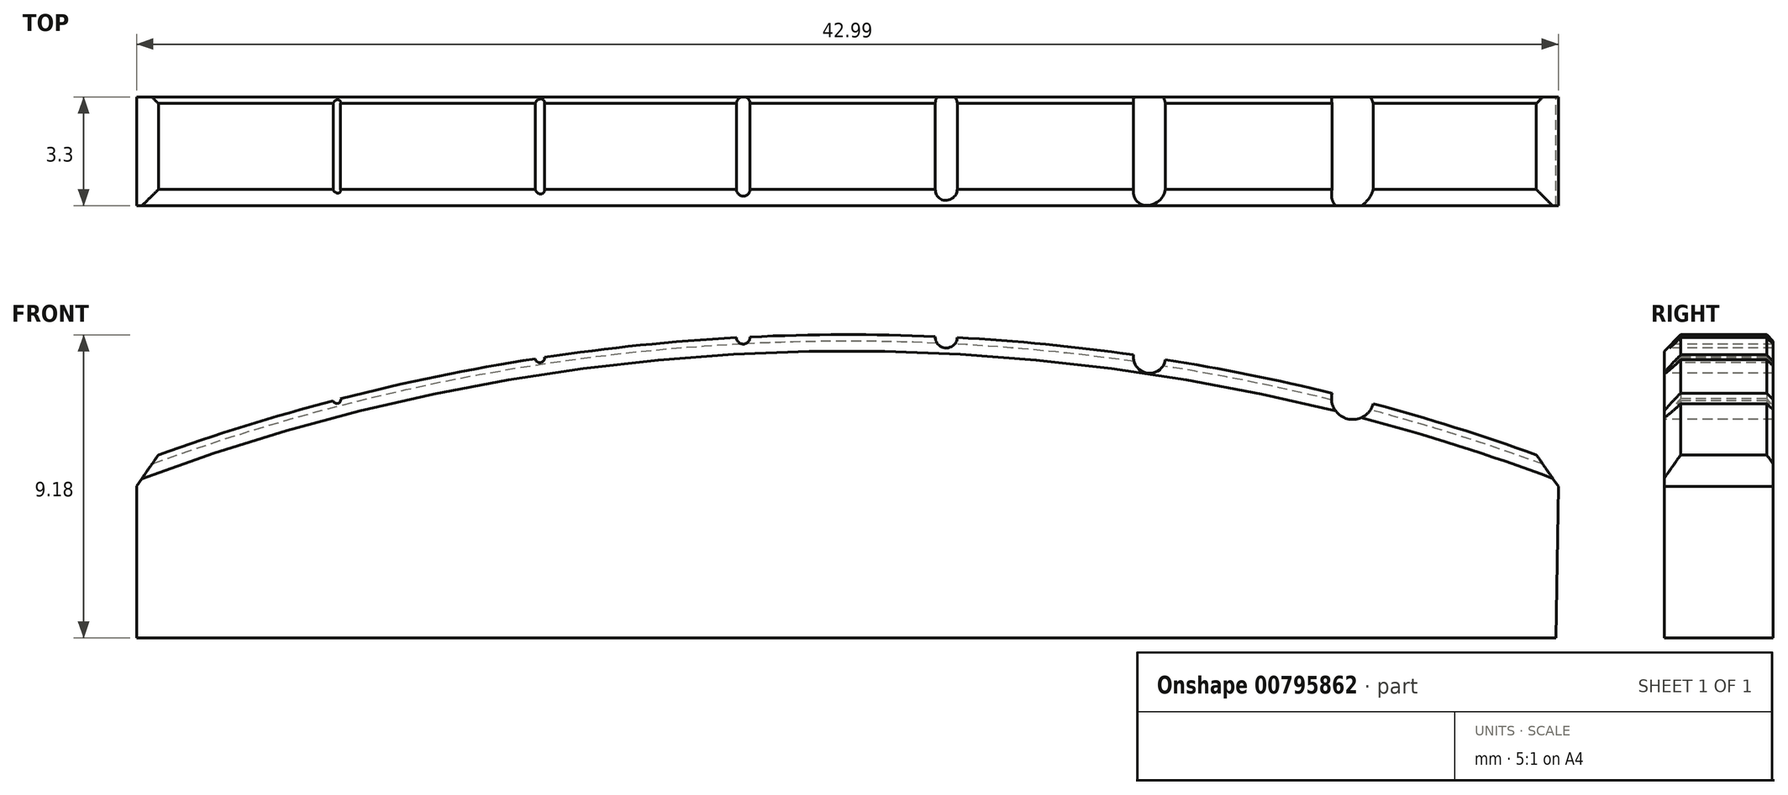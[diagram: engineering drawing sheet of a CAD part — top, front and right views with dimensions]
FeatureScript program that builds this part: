
annotation { "Feature Type Name" : "Feature", "Feature Type Description" : "" }
export const myFeature = defineFeature(function(context is Context, id is Id, definition is map)
    precondition{}
    {
        {
            var Q0;
            Q0=qCreatedBy(makeId("Front.planeOp"),FACE);
            var sketch = newSketch(context, id + "F0", { "sketchPlane" : qUnion([Q0])});
            skArc(sketch, "E0", {"start": v(-21.5, 5.3) * mm, "mid": v(0, 9.18) * mm, "end": v(21.5, 5.3) * mm});
            skLineSegment(sketch, "E1", {"start": v(-21.5, 5.3) * mm, "end": v(-21.5, 0) * mm});
            skLineSegment(sketch, "E2", {"start": v(-21.5, 0) * mm, "end": v(21.41, 0) * mm});
            skLineSegment(sketch, "E3", {"start": v(21.41, 0) * mm, "end": v(21.5, 5.3) * mm});
            skSolve(sketch);
        }
        {
            var Q0;
            Q0 = qSketchRegion(id + "F0", true);
            extrude(context, id + "F1", {"entities" : qUnion([Q0]), "depth" : 3.3 * mm, "offsetDistance" : 25 * mm});
        }
        {
            var Q0;
            Q0=makeQuery(id+"F1.opExtrude","CAP_FACE",FACE,{"disambiguationData":[OSD([sQuery(id+"F0.wireOp",EDGE,"E0"),sQuery(id+"F0.wireOp",EDGE,"E1"),sQuery(id+"F0.wireOp",EDGE,"E2"),sQuery(id+"F0.wireOp",EDGE,"E3")])],"isStart":false});
            var sketch = newSketch(context, id + "F2", { "sketchPlane" : qUnion([Q0])});
            skCircle(sketch, "E4", {"center": v(-15.44, 7.21) * mm, "radius": 0.12 * mm});
            skCircle(sketch, "E5", {"center": v(-9.3, 8.48) * mm, "radius": 0.14 * mm});
            skCircle(sketch, "E6", {"center": v(-3.16, 9.1) * mm, "radius": 0.2 * mm});
            skCircle(sketch, "E7", {"center": v(2.99, 9.11) * mm, "radius": 0.33 * mm});
            skCircle(sketch, "E8", {"center": v(9.13, 8.5) * mm, "radius": 0.49 * mm});
            skCircle(sketch, "E9", {"center": v(15.27, 7.26) * mm, "radius": 0.64 * mm});
            skLineSegment(sketch, "E10", {"start": v(-15.44, 7.21) * mm, "end": v(-15.44, 0) * mm, "construction": true});
            skLineSegment(sketch, "E11", {"start": v(-9.3, 8.48) * mm, "end": v(-9.3, 0) * mm, "construction": true});
            skLineSegment(sketch, "E12", {"start": v(-3.16, 9.1) * mm, "end": v(-3.16, 0) * mm, "construction": true});
            skLineSegment(sketch, "E13", {"start": v(2.99, 9.11) * mm, "end": v(2.99, 0) * mm, "construction": true});
            skLineSegment(sketch, "E14", {"start": v(9.13, 8.5) * mm, "end": v(9.13, 0) * mm, "construction": true});
            skLineSegment(sketch, "E15", {"start": v(15.27, 7.26) * mm, "end": v(15.27, 0) * mm, "construction": true});
            skSolve(sketch);
        }
        {
            var Q0;
            Q0 = qSketchRegion(id + "F2", true);
            extrude(context, id + "F3", {"entities" : qUnion([Q0]), "operationType" : NewBodyOperationType.REMOVE, "oppositeDirection" : true, "depth" : 25 * mm, "offsetDistance" : 25 * mm});
        }
        {
            var Q0;
            {var subQ0=sQuery(id+"F0.wireOp",EDGE,"E0");var subQ1=sQuery(id+"F0.wireOp",EDGE,"E1");Q0=makeQuery(id+"F3.boolean.opBoolean","SPLIT",EDGE,{"disambiguationData":[TD([makeQuery(id+"F1.opExtrude","SWEPT_FACE",FACE,{"disambiguationData":[OSD([subQ0])]}),makeQuery(id+"F1.opExtrude","CAP_FACE",FACE,{"disambiguationData":[OSD([subQ0,subQ1,sQuery(id+"F0.wireOp",EDGE,"E2"),sQuery(id+"F0.wireOp",EDGE,"E3")])],"isStart":false}),makeQuery(id+"F1.opExtrude","SWEPT_FACE",FACE,{"disambiguationData":[OSD([subQ1])]}),makeQuery(id+"F3.opExtrude","SWEPT_FACE",FACE,{"disambiguationData":[OSD([sQuery(id+"F2.wireOp",EDGE,"E4")])]})])],"derivedFrom":makeQuery(id+"F1.opExtrude","CAP_EDGE",EDGE,{"disambiguationData":[OSD([subQ0])],"isStart":false})});}
            var Q1;
            {var subQ0=sQuery(id+"F0.wireOp",EDGE,"E0");Q1=makeQuery(id+"F3.boolean.opBoolean","SPLIT",EDGE,{"disambiguationData":[TD([makeQuery(id+"F1.opExtrude","SWEPT_FACE",FACE,{"disambiguationData":[OSD([subQ0])]}),makeQuery(id+"F1.opExtrude","CAP_FACE",FACE,{"disambiguationData":[OSD([subQ0,sQuery(id+"F0.wireOp",EDGE,"E1"),sQuery(id+"F0.wireOp",EDGE,"E2"),sQuery(id+"F0.wireOp",EDGE,"E3")])],"isStart":false}),makeQuery(id+"F3.opExtrude","SWEPT_FACE",FACE,{"disambiguationData":[OSD([sQuery(id+"F2.wireOp",EDGE,"E4")])]}),makeQuery(id+"F3.opExtrude","SWEPT_FACE",FACE,{"disambiguationData":[OSD([sQuery(id+"F2.wireOp",EDGE,"E5")])]})])],"derivedFrom":makeQuery(id+"F1.opExtrude","CAP_EDGE",EDGE,{"disambiguationData":[OSD([subQ0])],"isStart":false})});}
            var Q2;
            {var subQ0=sQuery(id+"F0.wireOp",EDGE,"E0");Q2=makeQuery(id+"F3.boolean.opBoolean","SPLIT",EDGE,{"disambiguationData":[TD([makeQuery(id+"F1.opExtrude","SWEPT_FACE",FACE,{"disambiguationData":[OSD([subQ0])]}),makeQuery(id+"F1.opExtrude","CAP_FACE",FACE,{"disambiguationData":[OSD([subQ0,sQuery(id+"F0.wireOp",EDGE,"E1"),sQuery(id+"F0.wireOp",EDGE,"E2"),sQuery(id+"F0.wireOp",EDGE,"E3")])],"isStart":false}),makeQuery(id+"F3.opExtrude","SWEPT_FACE",FACE,{"disambiguationData":[OSD([sQuery(id+"F2.wireOp",EDGE,"E5")])]}),makeQuery(id+"F3.opExtrude","SWEPT_FACE",FACE,{"disambiguationData":[OSD([sQuery(id+"F2.wireOp",EDGE,"E6")])]})])],"derivedFrom":makeQuery(id+"F1.opExtrude","CAP_EDGE",EDGE,{"disambiguationData":[OSD([subQ0])],"isStart":false})});}
            var Q3;
            {var subQ0=sQuery(id+"F0.wireOp",EDGE,"E0");Q3=makeQuery(id+"F3.boolean.opBoolean","SPLIT",EDGE,{"disambiguationData":[TD([makeQuery(id+"F1.opExtrude","SWEPT_FACE",FACE,{"disambiguationData":[OSD([subQ0])]}),makeQuery(id+"F1.opExtrude","CAP_FACE",FACE,{"disambiguationData":[OSD([subQ0,sQuery(id+"F0.wireOp",EDGE,"E1"),sQuery(id+"F0.wireOp",EDGE,"E2"),sQuery(id+"F0.wireOp",EDGE,"E3")])],"isStart":false}),makeQuery(id+"F3.opExtrude","SWEPT_FACE",FACE,{"disambiguationData":[OSD([sQuery(id+"F2.wireOp",EDGE,"E6")])]}),makeQuery(id+"F3.opExtrude","SWEPT_FACE",FACE,{"disambiguationData":[OSD([sQuery(id+"F2.wireOp",EDGE,"E7")])]})])],"derivedFrom":makeQuery(id+"F1.opExtrude","CAP_EDGE",EDGE,{"disambiguationData":[OSD([subQ0])],"isStart":false})});}
            var Q4;
            {var subQ0=sQuery(id+"F0.wireOp",EDGE,"E0");Q4=makeQuery(id+"F3.boolean.opBoolean","SPLIT",EDGE,{"disambiguationData":[TD([makeQuery(id+"F1.opExtrude","SWEPT_FACE",FACE,{"disambiguationData":[OSD([subQ0])]}),makeQuery(id+"F1.opExtrude","CAP_FACE",FACE,{"disambiguationData":[OSD([subQ0,sQuery(id+"F0.wireOp",EDGE,"E1"),sQuery(id+"F0.wireOp",EDGE,"E2"),sQuery(id+"F0.wireOp",EDGE,"E3")])],"isStart":false}),makeQuery(id+"F3.opExtrude","SWEPT_FACE",FACE,{"disambiguationData":[OSD([sQuery(id+"F2.wireOp",EDGE,"E7")])]}),makeQuery(id+"F3.opExtrude","SWEPT_FACE",FACE,{"disambiguationData":[OSD([sQuery(id+"F2.wireOp",EDGE,"E8")])]})])],"derivedFrom":makeQuery(id+"F1.opExtrude","CAP_EDGE",EDGE,{"disambiguationData":[OSD([subQ0])],"isStart":false})});}
            var Q5;
            {var subQ0=sQuery(id+"F0.wireOp",EDGE,"E0");Q5=makeQuery(id+"F3.boolean.opBoolean","SPLIT",EDGE,{"disambiguationData":[TD([makeQuery(id+"F1.opExtrude","SWEPT_FACE",FACE,{"disambiguationData":[OSD([subQ0])]}),makeQuery(id+"F1.opExtrude","CAP_FACE",FACE,{"disambiguationData":[OSD([subQ0,sQuery(id+"F0.wireOp",EDGE,"E1"),sQuery(id+"F0.wireOp",EDGE,"E2"),sQuery(id+"F0.wireOp",EDGE,"E3")])],"isStart":false}),makeQuery(id+"F3.opExtrude","SWEPT_FACE",FACE,{"disambiguationData":[OSD([sQuery(id+"F2.wireOp",EDGE,"E8")])]}),makeQuery(id+"F3.opExtrude","SWEPT_FACE",FACE,{"disambiguationData":[OSD([sQuery(id+"F2.wireOp",EDGE,"E9")])]})])],"derivedFrom":makeQuery(id+"F1.opExtrude","CAP_EDGE",EDGE,{"disambiguationData":[OSD([subQ0])],"isStart":false})});}
            var Q6;
            {var subQ0=sQuery(id+"F0.wireOp",EDGE,"E0");var subQ1=sQuery(id+"F0.wireOp",EDGE,"E3");Q6=makeQuery(id+"F3.boolean.opBoolean","SPLIT",EDGE,{"disambiguationData":[TD([makeQuery(id+"F1.opExtrude","SWEPT_FACE",FACE,{"disambiguationData":[OSD([subQ0])]}),makeQuery(id+"F1.opExtrude","CAP_FACE",FACE,{"disambiguationData":[OSD([subQ0,sQuery(id+"F0.wireOp",EDGE,"E1"),sQuery(id+"F0.wireOp",EDGE,"E2"),subQ1])],"isStart":false}),makeQuery(id+"F1.opExtrude","SWEPT_FACE",FACE,{"disambiguationData":[OSD([subQ1])]}),makeQuery(id+"F3.opExtrude","SWEPT_FACE",FACE,{"disambiguationData":[OSD([sQuery(id+"F2.wireOp",EDGE,"E9")])]})])],"derivedFrom":makeQuery(id+"F1.opExtrude","CAP_EDGE",EDGE,{"disambiguationData":[OSD([subQ0])],"isStart":false})});}
            chamfer(context, id + "F4", {"entities" : qUnion([Q0, Q1, Q2, Q3, Q4, Q5, Q6]), "width" : 0.5 * mm, "tangentPropagation" : true});
        }
        {
            var Q0;
            {var subQ0=sQuery(id+"F0.wireOp",EDGE,"E0");var subQ1=sQuery(id+"F0.wireOp",EDGE,"E3");Q0=makeQuery(id+"F3.boolean.opBoolean","SPLIT",EDGE,{"disambiguationData":[TD([makeQuery(id+"F1.opExtrude","SWEPT_FACE",FACE,{"disambiguationData":[OSD([subQ0])]}),makeQuery(id+"F1.opExtrude","CAP_FACE",FACE,{"disambiguationData":[OSD([subQ0,sQuery(id+"F0.wireOp",EDGE,"E1"),sQuery(id+"F0.wireOp",EDGE,"E2"),subQ1])],"isStart":true}),makeQuery(id+"F1.opExtrude","SWEPT_FACE",FACE,{"disambiguationData":[OSD([subQ1])]}),makeQuery(id+"F3.opExtrude","SWEPT_FACE",FACE,{"disambiguationData":[OSD([sQuery(id+"F2.wireOp",EDGE,"E9")])]})])],"derivedFrom":makeQuery(id+"F1.opExtrude","CAP_EDGE",EDGE,{"disambiguationData":[OSD([subQ0])],"isStart":true})});}
            var Q1;
            {var subQ0=sQuery(id+"F0.wireOp",EDGE,"E0");Q1=makeQuery(id+"F3.boolean.opBoolean","SPLIT",EDGE,{"disambiguationData":[TD([makeQuery(id+"F1.opExtrude","SWEPT_FACE",FACE,{"disambiguationData":[OSD([subQ0])]}),makeQuery(id+"F1.opExtrude","CAP_FACE",FACE,{"disambiguationData":[OSD([subQ0,sQuery(id+"F0.wireOp",EDGE,"E1"),sQuery(id+"F0.wireOp",EDGE,"E2"),sQuery(id+"F0.wireOp",EDGE,"E3")])],"isStart":true}),makeQuery(id+"F3.opExtrude","SWEPT_FACE",FACE,{"disambiguationData":[OSD([sQuery(id+"F2.wireOp",EDGE,"E8")])]}),makeQuery(id+"F3.opExtrude","SWEPT_FACE",FACE,{"disambiguationData":[OSD([sQuery(id+"F2.wireOp",EDGE,"E9")])]})])],"derivedFrom":makeQuery(id+"F1.opExtrude","CAP_EDGE",EDGE,{"disambiguationData":[OSD([subQ0])],"isStart":true})});}
            var Q2;
            {var subQ0=sQuery(id+"F0.wireOp",EDGE,"E0");Q2=makeQuery(id+"F3.boolean.opBoolean","SPLIT",EDGE,{"disambiguationData":[TD([makeQuery(id+"F1.opExtrude","SWEPT_FACE",FACE,{"disambiguationData":[OSD([subQ0])]}),makeQuery(id+"F1.opExtrude","CAP_FACE",FACE,{"disambiguationData":[OSD([subQ0,sQuery(id+"F0.wireOp",EDGE,"E1"),sQuery(id+"F0.wireOp",EDGE,"E2"),sQuery(id+"F0.wireOp",EDGE,"E3")])],"isStart":true}),makeQuery(id+"F3.opExtrude","SWEPT_FACE",FACE,{"disambiguationData":[OSD([sQuery(id+"F2.wireOp",EDGE,"E7")])]}),makeQuery(id+"F3.opExtrude","SWEPT_FACE",FACE,{"disambiguationData":[OSD([sQuery(id+"F2.wireOp",EDGE,"E8")])]})])],"derivedFrom":makeQuery(id+"F1.opExtrude","CAP_EDGE",EDGE,{"disambiguationData":[OSD([subQ0])],"isStart":true})});}
            var Q3;
            {var subQ0=sQuery(id+"F0.wireOp",EDGE,"E0");Q3=makeQuery(id+"F3.boolean.opBoolean","SPLIT",EDGE,{"disambiguationData":[TD([makeQuery(id+"F1.opExtrude","SWEPT_FACE",FACE,{"disambiguationData":[OSD([subQ0])]}),makeQuery(id+"F1.opExtrude","CAP_FACE",FACE,{"disambiguationData":[OSD([subQ0,sQuery(id+"F0.wireOp",EDGE,"E1"),sQuery(id+"F0.wireOp",EDGE,"E2"),sQuery(id+"F0.wireOp",EDGE,"E3")])],"isStart":true}),makeQuery(id+"F3.opExtrude","SWEPT_FACE",FACE,{"disambiguationData":[OSD([sQuery(id+"F2.wireOp",EDGE,"E6")])]}),makeQuery(id+"F3.opExtrude","SWEPT_FACE",FACE,{"disambiguationData":[OSD([sQuery(id+"F2.wireOp",EDGE,"E7")])]})])],"derivedFrom":makeQuery(id+"F1.opExtrude","CAP_EDGE",EDGE,{"disambiguationData":[OSD([subQ0])],"isStart":true})});}
            var Q4;
            {var subQ0=sQuery(id+"F0.wireOp",EDGE,"E0");Q4=makeQuery(id+"F3.boolean.opBoolean","SPLIT",EDGE,{"disambiguationData":[TD([makeQuery(id+"F1.opExtrude","SWEPT_FACE",FACE,{"disambiguationData":[OSD([subQ0])]}),makeQuery(id+"F1.opExtrude","CAP_FACE",FACE,{"disambiguationData":[OSD([subQ0,sQuery(id+"F0.wireOp",EDGE,"E1"),sQuery(id+"F0.wireOp",EDGE,"E2"),sQuery(id+"F0.wireOp",EDGE,"E3")])],"isStart":true}),makeQuery(id+"F3.opExtrude","SWEPT_FACE",FACE,{"disambiguationData":[OSD([sQuery(id+"F2.wireOp",EDGE,"E5")])]}),makeQuery(id+"F3.opExtrude","SWEPT_FACE",FACE,{"disambiguationData":[OSD([sQuery(id+"F2.wireOp",EDGE,"E6")])]})])],"derivedFrom":makeQuery(id+"F1.opExtrude","CAP_EDGE",EDGE,{"disambiguationData":[OSD([subQ0])],"isStart":true})});}
            var Q5;
            {var subQ0=sQuery(id+"F0.wireOp",EDGE,"E0");Q5=makeQuery(id+"F3.boolean.opBoolean","SPLIT",EDGE,{"disambiguationData":[TD([makeQuery(id+"F1.opExtrude","SWEPT_FACE",FACE,{"disambiguationData":[OSD([subQ0])]}),makeQuery(id+"F1.opExtrude","CAP_FACE",FACE,{"disambiguationData":[OSD([subQ0,sQuery(id+"F0.wireOp",EDGE,"E1"),sQuery(id+"F0.wireOp",EDGE,"E2"),sQuery(id+"F0.wireOp",EDGE,"E3")])],"isStart":true}),makeQuery(id+"F3.opExtrude","SWEPT_FACE",FACE,{"disambiguationData":[OSD([sQuery(id+"F2.wireOp",EDGE,"E4")])]}),makeQuery(id+"F3.opExtrude","SWEPT_FACE",FACE,{"disambiguationData":[OSD([sQuery(id+"F2.wireOp",EDGE,"E5")])]})])],"derivedFrom":makeQuery(id+"F1.opExtrude","CAP_EDGE",EDGE,{"disambiguationData":[OSD([subQ0])],"isStart":true})});}
            var Q6;
            {var subQ0=sQuery(id+"F0.wireOp",EDGE,"E0");var subQ1=sQuery(id+"F0.wireOp",EDGE,"E1");Q6=makeQuery(id+"F3.boolean.opBoolean","SPLIT",EDGE,{"disambiguationData":[TD([makeQuery(id+"F1.opExtrude","SWEPT_FACE",FACE,{"disambiguationData":[OSD([subQ0])]}),makeQuery(id+"F1.opExtrude","CAP_FACE",FACE,{"disambiguationData":[OSD([subQ0,subQ1,sQuery(id+"F0.wireOp",EDGE,"E2"),sQuery(id+"F0.wireOp",EDGE,"E3")])],"isStart":true}),makeQuery(id+"F1.opExtrude","SWEPT_FACE",FACE,{"disambiguationData":[OSD([subQ1])]}),makeQuery(id+"F3.opExtrude","SWEPT_FACE",FACE,{"disambiguationData":[OSD([sQuery(id+"F2.wireOp",EDGE,"E4")])]})])],"derivedFrom":makeQuery(id+"F1.opExtrude","CAP_EDGE",EDGE,{"disambiguationData":[OSD([subQ0])],"isStart":true})});}
            chamfer(context, id + "F5", {"entities" : qUnion([Q0, Q1, Q2, Q3, Q4, Q5, Q6]), "width" : 0.2 * mm, "tangentPropagation" : true});
        }
        {
            var Q0;
            Q0=makeQuery(id+"F1.opExtrude","SWEPT_EDGE",EDGE,{"disambiguationData":[OSD([sQuery(id+"F0.wireOp",EDGE,"E0"),sQuery(id+"F0.wireOp",EDGE,"E3")])]});
            var Q1;
            Q1=makeQuery(id+"F1.opExtrude","SWEPT_EDGE",EDGE,{"disambiguationData":[OSD([sQuery(id+"F0.wireOp",EDGE,"E0"),sQuery(id+"F0.wireOp",EDGE,"E1")])]});
            chamfer(context, id + "F6", {"entities" : qUnion([Q0, Q1]), "width" : 1 * mm, "tangentPropagation" : true});
        }
    });
